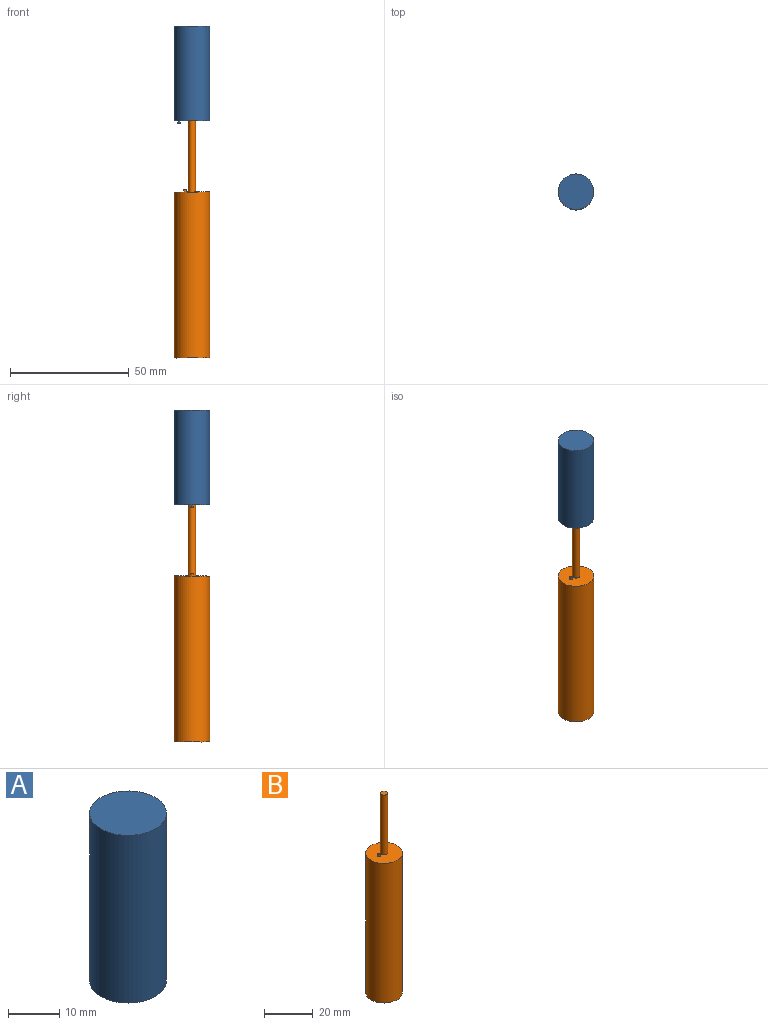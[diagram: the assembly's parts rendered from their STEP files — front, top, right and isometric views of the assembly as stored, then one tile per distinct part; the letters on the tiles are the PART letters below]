
ASSEMBLY  parts=2 mates=1
PART A: 7 faces, bbox 15x15x41 mm
  f0: cylinder r=7.5mm len=40mm, axis (0,0,-1), area 1885mm2, adj f1,f2
  f1: plane 15x15mm, normal (0,0,1), area 176.7mm2, adj f0
  f2: plane 15x15mm, normal (0,0,-1), area 166.8mm2, adj f0,f3,f5
  f3: cylinder r=1.7mm len=35mm, axis (0,0,-1), area 373.8mm2, adj f2,f4
  f4: plane 3.4x3.4mm, normal (0,0,-1), area 9.1mm2, adj f3
  f5: cylinder r=0.5mm len=1mm, axis (0,0,1), area 3.1mm2, adj f2,f6
  f6: plane 1x1mm, normal (0,0,-1), area 0.8mm2, adj f5
PART B: 7 faces, bbox 15x15x100 mm
  f0: cylinder r=7.5mm len=70mm, axis (0,0,-1), area 3298.7mm2, adj f1,f2
  f1: plane 15x15mm, normal (0,0,1), area 168.9mm2, adj f0,f3,f5
  f2: plane 15x15mm, normal (0,0,-1), area 176.7mm2, adj f0
  f3: cylinder r=1.5mm len=30mm, axis (0,0,-1), area 282.7mm2, adj f1,f4
  f4: plane 3x3mm, normal (0,0,1), area 7.1mm2, adj f3
  f5: cylinder r=0.5mm len=1mm, axis (0,0,-1), area 3.1mm2, adj f1,f6
  f6: plane 1x1mm, normal (0,0,1), area 0.8mm2, adj f5
PLACE A rot(axis=(0.46,-0.81,0.36),0deg) t=(-33.06,-23.56,68.63)mm
PLACE B rot(axis=(0.46,-0.81,0.36),0deg) t=(-33.06,-23.56,-31.37)mm
MATE slider A.f0 <-> B.f3  axis (0,0,-1) through (-33.06,-23.56,68.63)mm
